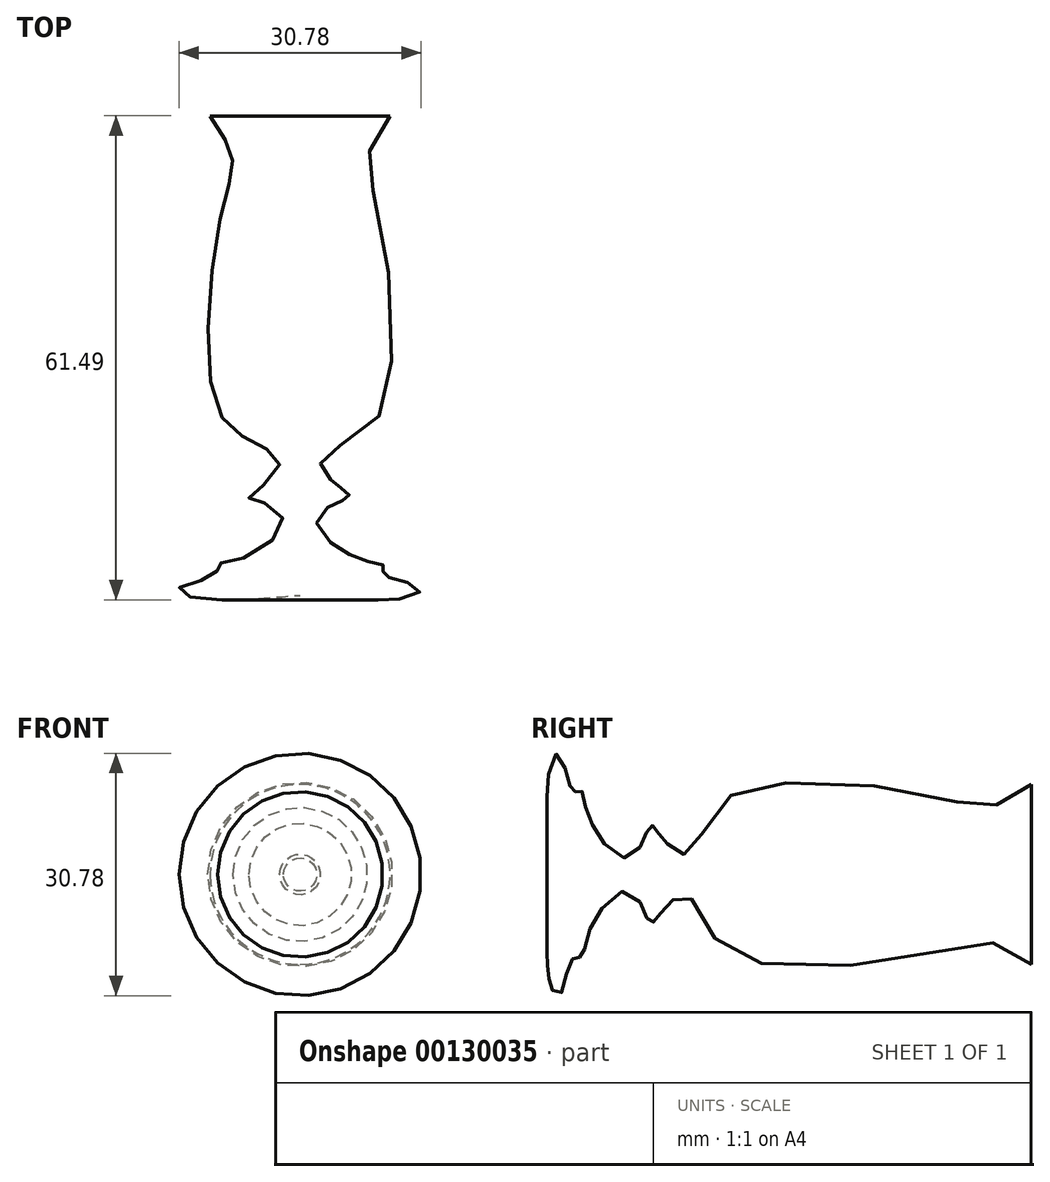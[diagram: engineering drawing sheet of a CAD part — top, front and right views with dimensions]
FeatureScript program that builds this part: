
annotation { "Feature Type Name" : "Feature", "Feature Type Description" : "" }
export const myFeature = defineFeature(function(context is Context, id is Id, definition is map)
    precondition{}
    {
        {
            var Q0;
            Q0=qCreatedBy(makeId("Top.planeOp"),FACE);
            var sketch = newSketch(context, id + "F0", { "sketchPlane" : qUnion([Q0])});
            skFitSpline(sketch, "E0", {"points": [v(-58.98, 63.7) * mm, v(-56.15, 58.43) * mm, v(-57.55, 51.4) * mm, v(-58.25, 27.02) * mm, v(-53.16, 22.1) * mm, v(-50.18, 19.13) * mm, v(-54.04, 15.27) * mm, v(-53.16, 14.91) * mm, v(-49.66, 12.1) * mm, v(-55.8, 7.2) * mm, v(-58.08, 6.67) * mm, v(-58.25, 5.44) * mm, v(-62.81, 3.86) * mm, v(-62.11, 2.8) * mm, v(-47.55, 2.8) * mm], "startDerivative": vector(49.27, -79.48) * mm, "endDerivative": vector(158.54, 13.23) * mm});
            skLineSegment(sketch, "E1", {"start": v(-47.55, 2.8) * mm, "end": v(-47.55, 22.24) * mm});
            skLineSegment(sketch, "E2", {"start": v(-47.55, 22.24) * mm, "end": v(-47.55, 63.7) * mm});
            skLineSegment(sketch, "E3", {"start": v(-47.55, 63.7) * mm, "end": v(-58.98, 63.7) * mm});
            skPoint(sketch, "E4.5.internal.orphan", {"position": v(-25.56, 0) * mm});
            skSolve(sketch);
        }
        {
            var Q0;
            Q0 = qSketchRegion(id + "F0", true);
            var Q1;
            Q1=sQuery(id+"F0.wireOp",EDGE,"E2");
            revolve(context, id + "F1", {"entities" : qUnion([Q0]), "axis" : qUnion([Q1]), "revolveType" : RevolveType.FULL});
        }
    });
